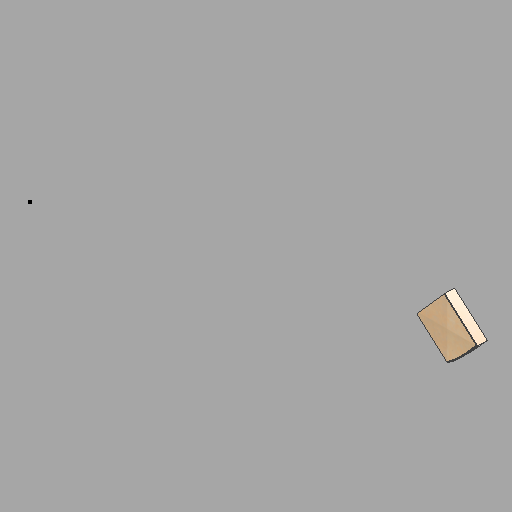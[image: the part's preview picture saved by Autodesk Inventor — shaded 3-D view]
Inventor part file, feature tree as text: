
AUTODESK INVENTOR PART (.ipt)
format: ipt  version: 2022.1 (Build 261234020, 234B)  size: 178,176 bytes
history: native  units: in
note: dims shown in document units (in); Inventor stores cm internally (conversion verified against a paired STEP export)
features: sketch x13, plane x4, other x3
ambient origin geometry x8: Origin, YZ Plane, XZ Plane, XY Plane, X Axis, Y Axis, Z Axis, Center Point
bodies: Solid1 (feature_tree)
feature tree (20):
  other  "Solid18.ipt"
  other  "Solid1::Solid18.ipt"
  other  "TaggingFeature1"
  sketch  "Sketch1"  dims[d0=0.3937in]
  sketch  "Sketch2"
  sketch  "Sketch3"
  sketch  "Sketch4"
  sketch  "Sketch5"
  sketch  "Sketch6"
  sketch  "Sketch12"
  sketch  "Sketch13"
  sketch  "Sketch14"
  sketch  "Sketch15"
  sketch  "Sketch16"
  sketch  "Sketch17"
  sketch  "Sketch19"
  plane  "Work Plane1"
  plane  "Work Plane2"
  plane  "Work Plane5"
  plane  "Work Plane6"
